# Revit family: Thorn DIFFALUX
name_source: partatom
category: Lighting Fixtures
revit_build: Autodesk Revit 2018 (Build: 20170223_1515(x64)
units: mm (PartAtom-declared; Revit-internal decimal feet)

## family parameters
Cut with Voids When Loaded = No
Host = Face
Light Source = Yes
OmniClass Number = 23.80.70.11
OmniClass Title = Luminaries for Internal Lighting
Part Type = Normal
Room Calculation Point = No
Round Connector Dimension = Use Diameter
Shared = No

## types (1)
- DIFF 3 5000-840 HF L1500 LOS
    Apparent Load = 44 VA
    Assembly Code = D5020200
    Color Filter = 16777215
    Cost = 0 $
    Default Elevation = 0 mm  [stored 0 ft]
    Description = Surface Mount LED luminaire
    Dimming Lamp Color Temperature Shift = <None>
    Emit Shape Visible in Rendering = No
    Emit from Rectangle Length = 1442 mm  [stored 4.73097 ft]
    Emit from Rectangle Width = 180 mm
    Height = 81 mm  [stored 0.265748 ft]
    Lamp = LED
    Length = 1490 mm  [stored 4.88845 ft]
    Manufacturer = Thorn Lighting
    Photometric Web File = 96633566_(res15_5_symC0_C90_LOR_100).IES
    Tilt Angle = -90.00°
    URL = www.thornlighting.com/96633566
    Voltage = 0 V
    Width = 200 mm  [stored 0.656168 ft]

note: [stored X ft] marks values corroborated as IEEE doubles in the binary element streams (Revit-internal decimal feet)

## geometry (parser evidence)
native form markers: Sweep x2
no freeform markers — native parametric forms only
